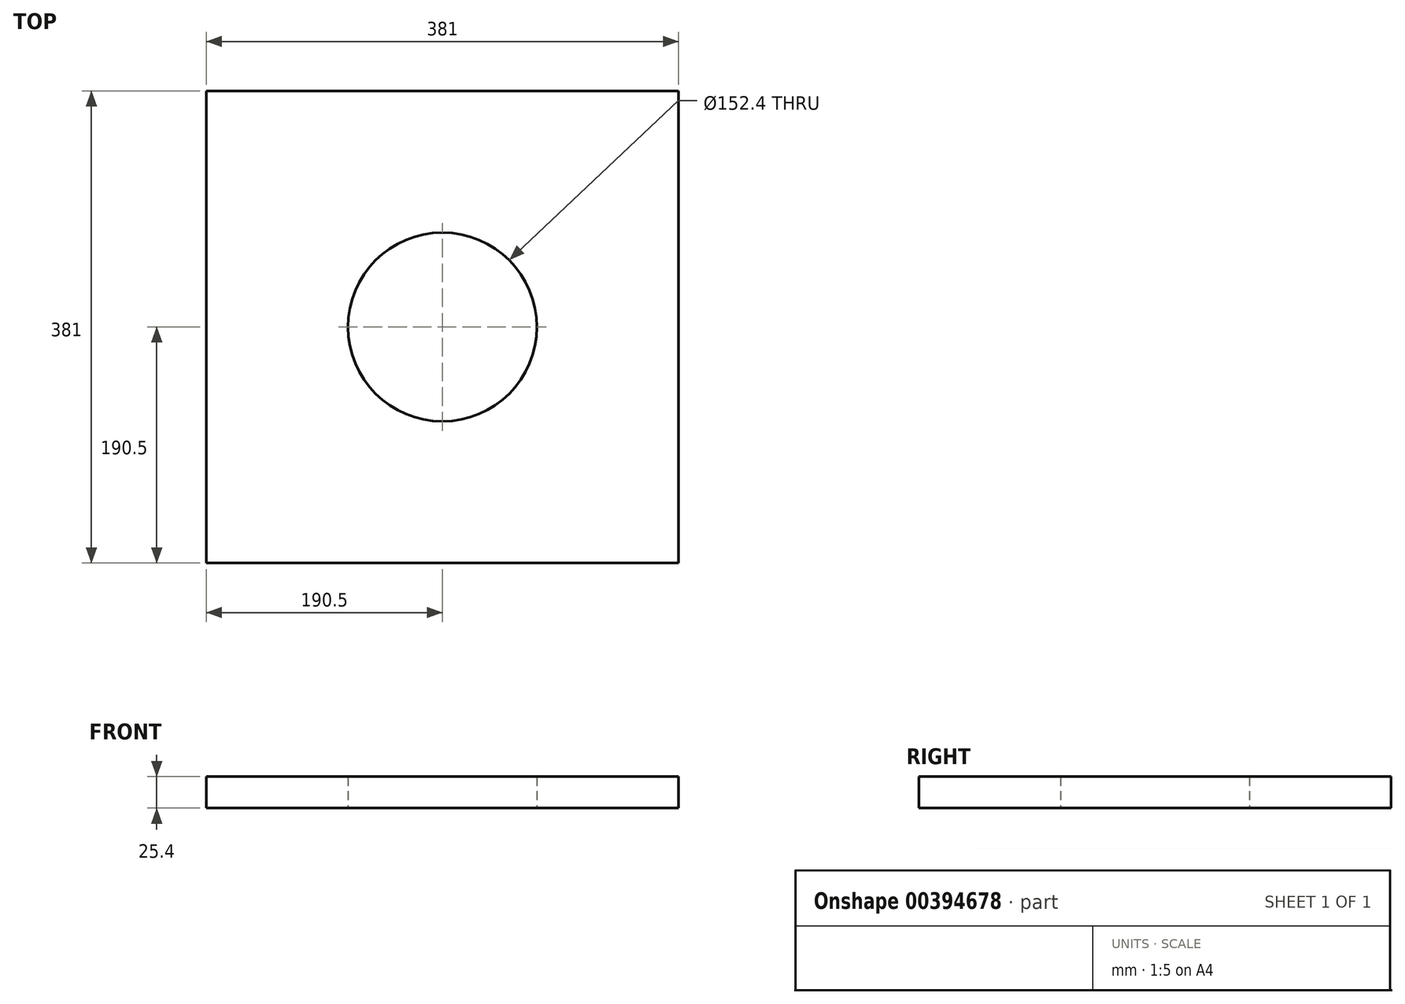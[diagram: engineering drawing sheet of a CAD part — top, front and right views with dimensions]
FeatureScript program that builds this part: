
annotation { "Feature Type Name" : "Feature", "Feature Type Description" : "" }
export const myFeature = defineFeature(function(context is Context, id is Id, definition is map)
    precondition{}
    {
        {
            var Q0;
            Q0=qCreatedBy(makeId("Top.planeOp"),FACE);
            var sketch = newSketch(context, id + "F0", { "sketchPlane" : qUnion([Q0])});
            skLineSegment(sketch, "E0.bottom", {"start": v(-190.5, 190.5) * mm, "end": v(190.5, 190.5) * mm});
            skLineSegment(sketch, "E0.top", {"start": v(-190.5, -190.5) * mm, "end": v(190.5, -190.5) * mm});
            skLineSegment(sketch, "E0.left", {"start": v(-190.5, 190.5) * mm, "end": v(-190.5, -190.5) * mm});
            skLineSegment(sketch, "E0.right", {"start": v(190.5, 190.5) * mm, "end": v(190.5, -190.5) * mm});
            skPoint(sketch, "E0.middle", {"position": v(0, 0) * mm});
            skCircle(sketch, "E1", {"center": v(0, 0) * mm, "radius": 76.2 * mm});
            skSolve(sketch);
        }
        {
            var Q0;
            Q0=makeQuery(id+"F0.imprint","IMPRINT",FACE,{"disambiguationData":[TD([[makeQuery(id+"F0.imprint","IMPRINT",EDGE,{"derivedFrom":sQuery(id+"F0.wireOp",EDGE,"E0.bottom")}),-1.0]])]});
            extrude(context, id + "F1", {"entities" : qUnion([Q0]), "depth" : 25.4 * mm});
        }
    });
